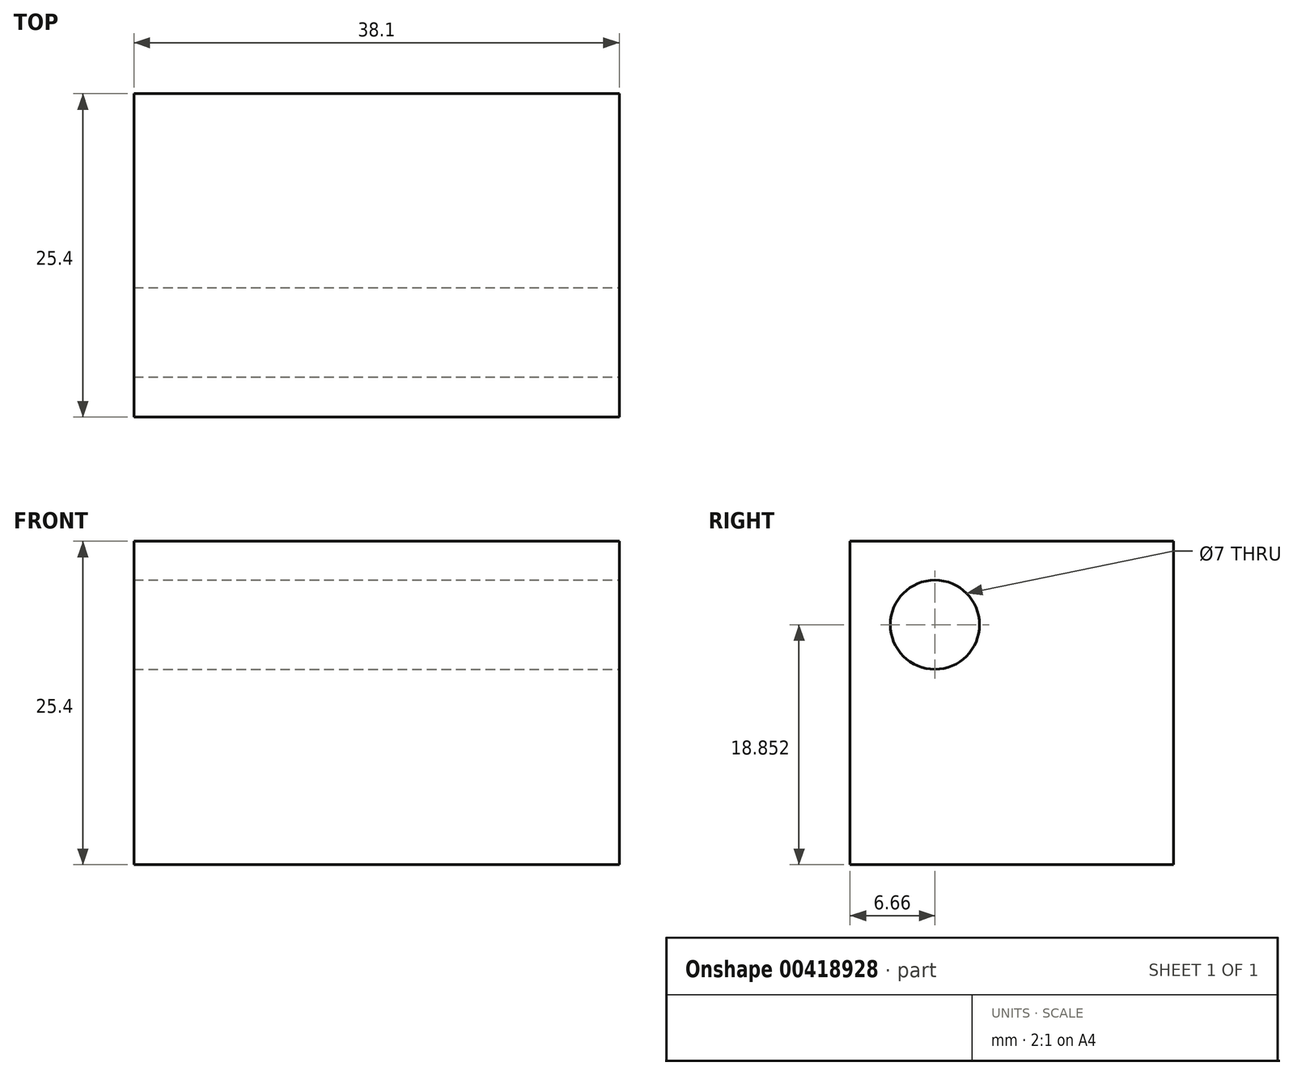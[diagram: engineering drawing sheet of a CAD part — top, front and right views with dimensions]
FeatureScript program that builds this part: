
annotation { "Feature Type Name" : "Feature", "Feature Type Description" : "" }
export const myFeature = defineFeature(function(context is Context, id is Id, definition is map)
    precondition{}
    {
        {
            var Q0;
            Q0=qCreatedBy(makeId("Top.planeOp"),FACE);
            var sketch = newSketch(context, id + "F0", { "sketchPlane" : qUnion([Q0])});
            skLineSegment(sketch, "E0", {"start": v(0, 0) * mm, "end": v(0, 25.4) * mm});
            skLineSegment(sketch, "E1", {"start": v(0, 25.4) * mm, "end": v(38.1, 25.4) * mm});
            skLineSegment(sketch, "E2", {"start": v(38.1, 25.4) * mm, "end": v(38.1, 0) * mm});
            skLineSegment(sketch, "E3", {"start": v(38.1, 0) * mm, "end": v(0, 0) * mm});
            skSolve(sketch);
        }
        {
            var Q0;
            Q0=makeQuery(id+"F0.imprint","IMPRINT",FACE,{"disambiguationData":[TD([[makeQuery(id+"F0.imprint","IMPRINT",EDGE,{"derivedFrom":sQuery(id+"F0.wireOp",EDGE,"E0")}),-1.0]])]});
            extrude(context, id + "F1", {"entities" : qUnion([Q0]), "depth" : 25.4 * mm});
        }
        {
            var Q0;
            Q0=makeQuery(id+"F1.opExtrude","SWEPT_FACE",FACE,{"disambiguationData":[OSD([sQuery(id+"F0.wireOp",EDGE,"E2")])]});
            var sketch = newSketch(context, id + "F2", { "sketchPlane" : qUnion([Q0])});
            skCircle(sketch, "E4", {"center": v(6.66, 18.85) * mm, "radius": 3.5 * mm});
            skSolve(sketch);
        }
        {
            var Q0;
            Q0=sQuery(id+"F2.wireOp",VERTEX,"E4.center");
            var Q1;
            Q1=makeQuery(id+"F1.opExtrude","SWEPT_BODY",BODY,{"disambiguationData":[OSD([sQuery(id+"F0.wireOp",EDGE,"E0"),sQuery(id+"F0.wireOp",EDGE,"E1"),sQuery(id+"F0.wireOp",EDGE,"E2"),sQuery(id+"F0.wireOp",EDGE,"E3")])]});
            hole(context, id + "F3", {"style" : HoleStyle.SIMPLE, "endStyle" : HoleEndStyle.THROUGH, "holeDiameter" : 7 * mm, "isTappedThrough" : true, "tappedDepth" : 12.7 * mm, "tapClearance" : 3, "locations" : qUnion([Q0]), "scope" : qUnion([Q1])});
        }
    });
